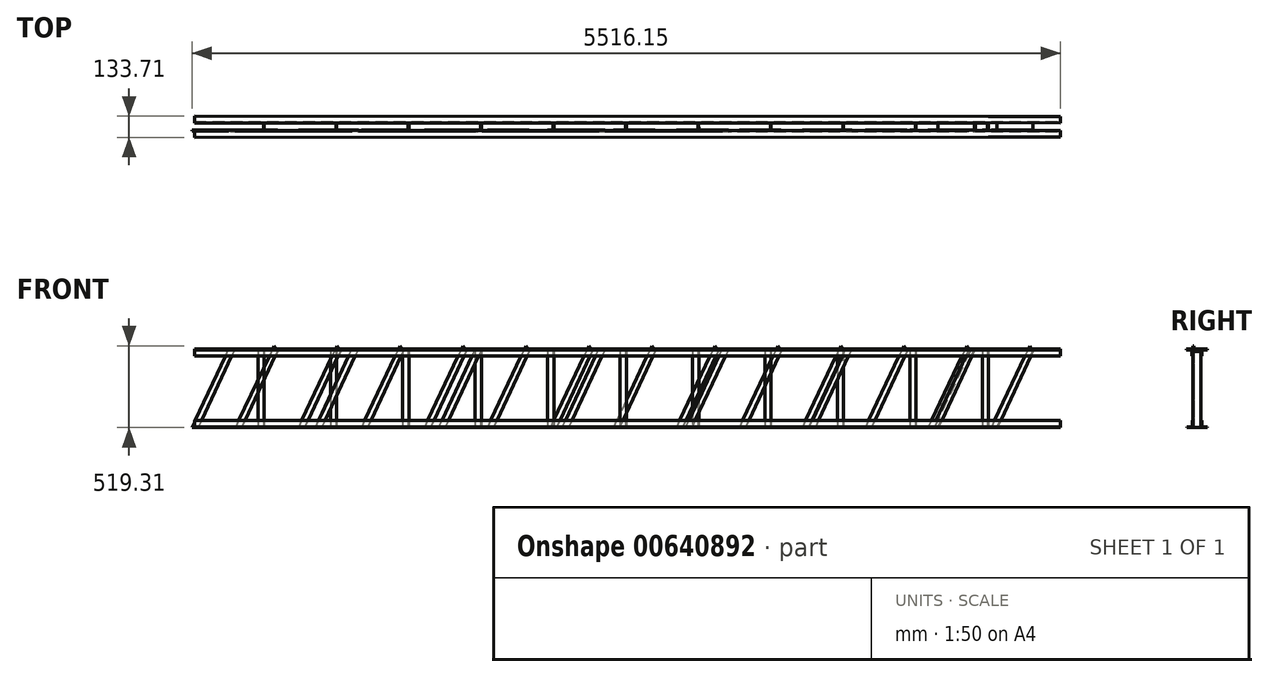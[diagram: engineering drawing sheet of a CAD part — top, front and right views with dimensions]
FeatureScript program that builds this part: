
annotation { "Feature Type Name" : "Feature", "Feature Type Description" : "" }
export const myFeature = defineFeature(function(context is Context, id is Id, definition is map)
    precondition{}
    {
        {
            var Q0;
            Q0=qCreatedBy(makeId("Top.planeOp"),FACE);
            var sketch = newSketch(context, id + "F0", { "sketchPlane" : qUnion([Q0])});
            skLineSegment(sketch, "E0.bottom", {"start": v(-72.3, 14.48) * mm, "end": v(5427.7, 14.48) * mm});
            skLineSegment(sketch, "E0.top", {"start": v(-72.3, -25.52) * mm, "end": v(5427.7, -25.52) * mm});
            skLineSegment(sketch, "E0.left", {"start": v(-72.3, 14.48) * mm, "end": v(-72.3, -25.52) * mm});
            skLineSegment(sketch, "E0.right", {"start": v(5427.7, 14.48) * mm, "end": v(5427.7, -25.52) * mm});
            skSolve(sketch);
        }
        {
            var Q0;
            Q0 = qSketchRegion(id + "F0", true);
            extrude(context, id + "F1", {"entities" : qUnion([Q0]), "depth" : 5 * mm, "offsetDistance" : 25.4 * mm});
        }
        {
            var Q0;
            Q0=makeQuery(id+"F1.opExtrude","CAP_FACE",FACE,{"disambiguationData":[OSD([sQuery(id+"F0.wireOp",EDGE,"E0.bottom"),sQuery(id+"F0.wireOp",EDGE,"E0.top"),sQuery(id+"F0.wireOp",EDGE,"E0.left"),sQuery(id+"F0.wireOp",EDGE,"E0.right")])],"isStart":false});
            var sketch = newSketch(context, id + "F2", { "sketchPlane" : qUnion([Q0])});
            skLineSegment(sketch, "E1.bottom", {"start": v(-72.3, -25.52) * mm, "end": v(5427.7, -25.52) * mm});
            skLineSegment(sketch, "E1.top", {"start": v(-72.3, -20.52) * mm, "end": v(5427.7, -20.52) * mm});
            skLineSegment(sketch, "E1.left", {"start": v(-72.3, -25.52) * mm, "end": v(-72.3, -20.52) * mm});
            skLineSegment(sketch, "E1.right", {"start": v(5427.7, -25.52) * mm, "end": v(5427.7, -20.52) * mm});
            skSolve(sketch);
        }
        {
            var Q0;
            Q0 = qSketchRegion(id + "F2", true);
            extrude(context, id + "F3", {"entities" : qUnion([Q0]), "operationType" : NewBodyOperationType.ADD, "depth" : 40 * mm, "offsetDistance" : 25.4 * mm});
        }
        {
            var Q0;
            Q0=makeQuery(id+"F3.boolean.opBoolean","MERGE",FACE,{"derivedFrom":[makeQuery(id+"F1.opExtrude","SWEPT_FACE",FACE,{"disambiguationData":[OSD([sQuery(id+"F0.wireOp",EDGE,"E0.top")])]}),makeQuery(id+"F3.opExtrude","SWEPT_FACE",FACE,{"disambiguationData":[OSD([sQuery(id+"F2.wireOp",EDGE,"E1.bottom")])]})]});
            cPlane(context, id + "F4", {"entities" : qUnion([Q0]), "cplaneType" : CPlaneType.OFFSET, "offset" : 25 * mm, "width" : 152.4 * mm, "height" : 152.4 * mm});
        }
        {
            var Q0;
            Q0=makeQuery(id+"F1.opExtrude","SWEPT_BODY",BODY,{"disambiguationData":[OSD([sQuery(id+"F0.wireOp",EDGE,"E0.bottom"),sQuery(id+"F0.wireOp",EDGE,"E0.top"),sQuery(id+"F0.wireOp",EDGE,"E0.left"),sQuery(id+"F0.wireOp",EDGE,"E0.right")])]});
            var Q1;
            Q1=qCreatedBy(id+"F4.planeOp",FACE);
            mirror(context, id + "F5", {"entities" : qUnion([Q0]), "mirrorPlane" : qUnion([Q1])});
        }
        {
            var Q0;
            Q0=makeQuery(id+"F5.opPattern","COPY",FACE,{"derivedFrom":makeQuery(id+"F3.boolean.opBoolean","MERGE",FACE,{"derivedFrom":[makeQuery(id+"F1.opExtrude","SWEPT_FACE",FACE,{"disambiguationData":[OSD([sQuery(id+"F0.wireOp",EDGE,"E0.top")])]}),makeQuery(id+"F3.opExtrude","SWEPT_FACE",FACE,{"disambiguationData":[OSD([sQuery(id+"F2.wireOp",EDGE,"E1.bottom")])]})]}),"instanceName":"1"});
            var sketch = newSketch(context, id + "F6", { "sketchPlane" : qUnion([Q0])});
            skLineSegment(sketch, "E2", {"start": v(-5233.44, 519.3) * mm, "end": v(-5253.8, 484.87) * mm});
            skLineSegment(sketch, "E3", {"start": v(-5253.8, 484.87) * mm, "end": v(-5027.7, 0) * mm});
            skLineSegment(sketch, "E4", {"start": v(-5027.7, 0) * mm, "end": v(-4987.7, 0) * mm});
            skLineSegment(sketch, "E5", {"start": v(-5233.44, 519.3) * mm, "end": v(-4987.7, 0) * mm});
            skLineSegment(sketch, "E6.1.0.0", {"start": v(-4853.8, 484.87) * mm, "end": v(-4627.7, 0) * mm});
            skLineSegment(sketch, "E6.1.0.1", {"start": v(-4833.44, 519.3) * mm, "end": v(-4587.7, 0) * mm});
            skLineSegment(sketch, "E6.1.0.2", {"start": v(-4833.44, 519.3) * mm, "end": v(-4853.8, 484.87) * mm});
            skLineSegment(sketch, "E6.1.0.3", {"start": v(-4627.7, 0) * mm, "end": v(-4587.7, 0) * mm});
            skLineSegment(sketch, "E6.2.0.0", {"start": v(-4453.8, 484.87) * mm, "end": v(-4227.7, 0) * mm});
            skLineSegment(sketch, "E6.2.0.1", {"start": v(-4433.44, 519.3) * mm, "end": v(-4187.7, 0) * mm});
            skLineSegment(sketch, "E6.2.0.2", {"start": v(-4433.44, 519.3) * mm, "end": v(-4453.8, 484.87) * mm});
            skLineSegment(sketch, "E6.2.0.3", {"start": v(-4227.7, 0) * mm, "end": v(-4187.7, 0) * mm});
            skLineSegment(sketch, "E6.3.0.0", {"start": v(-4053.8, 484.87) * mm, "end": v(-3827.7, 0) * mm});
            skLineSegment(sketch, "E6.3.0.1", {"start": v(-4033.44, 519.3) * mm, "end": v(-3787.7, 0) * mm});
            skLineSegment(sketch, "E6.3.0.2", {"start": v(-4033.44, 519.3) * mm, "end": v(-4053.8, 484.87) * mm});
            skLineSegment(sketch, "E6.3.0.3", {"start": v(-3827.7, 0) * mm, "end": v(-3787.7, 0) * mm});
            skLineSegment(sketch, "E6.4.0.0", {"start": v(-3653.8, 484.87) * mm, "end": v(-3427.7, 0) * mm});
            skLineSegment(sketch, "E6.4.0.1", {"start": v(-3633.44, 519.3) * mm, "end": v(-3387.7, 0) * mm});
            skLineSegment(sketch, "E6.4.0.2", {"start": v(-3633.44, 519.3) * mm, "end": v(-3653.8, 484.87) * mm});
            skLineSegment(sketch, "E6.4.0.3", {"start": v(-3427.7, 0) * mm, "end": v(-3387.7, 0) * mm});
            skLineSegment(sketch, "E6.5.0.0", {"start": v(-3253.8, 484.87) * mm, "end": v(-3027.7, 0) * mm});
            skLineSegment(sketch, "E6.5.0.1", {"start": v(-3233.44, 519.3) * mm, "end": v(-2987.7, 0) * mm});
            skLineSegment(sketch, "E6.5.0.2", {"start": v(-3233.44, 519.3) * mm, "end": v(-3253.8, 484.87) * mm});
            skLineSegment(sketch, "E6.5.0.3", {"start": v(-3027.7, 0) * mm, "end": v(-2987.7, 0) * mm});
            skLineSegment(sketch, "E6.6.0.0", {"start": v(-2853.8, 484.87) * mm, "end": v(-2627.7, 0) * mm});
            skLineSegment(sketch, "E6.6.0.1", {"start": v(-2833.44, 519.3) * mm, "end": v(-2587.7, 0) * mm});
            skLineSegment(sketch, "E6.6.0.2", {"start": v(-2833.44, 519.3) * mm, "end": v(-2853.8, 484.87) * mm});
            skLineSegment(sketch, "E6.6.0.3", {"start": v(-2627.7, 0) * mm, "end": v(-2587.7, 0) * mm});
            skLineSegment(sketch, "E6.7.0.0", {"start": v(-2453.8, 484.87) * mm, "end": v(-2227.7, 0) * mm});
            skLineSegment(sketch, "E6.7.0.1", {"start": v(-2433.44, 519.3) * mm, "end": v(-2187.7, 0) * mm});
            skLineSegment(sketch, "E6.7.0.2", {"start": v(-2433.44, 519.3) * mm, "end": v(-2453.8, 484.87) * mm});
            skLineSegment(sketch, "E6.7.0.3", {"start": v(-2227.7, 0) * mm, "end": v(-2187.7, 0) * mm});
            skLineSegment(sketch, "E6.8.0.0", {"start": v(-2053.8, 484.87) * mm, "end": v(-1827.7, 0) * mm});
            skLineSegment(sketch, "E6.8.0.1", {"start": v(-2033.44, 519.3) * mm, "end": v(-1787.7, 0) * mm});
            skLineSegment(sketch, "E6.8.0.2", {"start": v(-2033.44, 519.3) * mm, "end": v(-2053.8, 484.87) * mm});
            skLineSegment(sketch, "E6.8.0.3", {"start": v(-1827.7, 0) * mm, "end": v(-1787.7, 0) * mm});
            skLineSegment(sketch, "E6.9.0.0", {"start": v(-1653.8, 484.87) * mm, "end": v(-1427.7, 0) * mm});
            skLineSegment(sketch, "E6.9.0.1", {"start": v(-1633.44, 519.3) * mm, "end": v(-1387.7, 0) * mm});
            skLineSegment(sketch, "E6.9.0.2", {"start": v(-1633.44, 519.3) * mm, "end": v(-1653.8, 484.87) * mm});
            skLineSegment(sketch, "E6.9.0.3", {"start": v(-1427.7, 0) * mm, "end": v(-1387.7, 0) * mm});
            skLineSegment(sketch, "E6.10.0.0", {"start": v(-1253.8, 484.87) * mm, "end": v(-1027.7, 0) * mm});
            skLineSegment(sketch, "E6.10.0.1", {"start": v(-1233.44, 519.3) * mm, "end": v(-987.7, 0) * mm});
            skLineSegment(sketch, "E6.10.0.2", {"start": v(-1233.44, 519.3) * mm, "end": v(-1253.8, 484.87) * mm});
            skLineSegment(sketch, "E6.10.0.3", {"start": v(-1027.7, 0) * mm, "end": v(-987.7, 0) * mm});
            skLineSegment(sketch, "E6.11.0.0", {"start": v(-853.8, 484.87) * mm, "end": v(-627.7, 0) * mm});
            skLineSegment(sketch, "E6.11.0.1", {"start": v(-833.44, 519.3) * mm, "end": v(-587.7, 0) * mm});
            skLineSegment(sketch, "E6.11.0.2", {"start": v(-833.44, 519.3) * mm, "end": v(-853.8, 484.87) * mm});
            skLineSegment(sketch, "E6.11.0.3", {"start": v(-627.7, 0) * mm, "end": v(-587.7, 0) * mm});
            skLineSegment(sketch, "E6.12.0.0", {"start": v(-453.8, 484.87) * mm, "end": v(-227.7, 0) * mm});
            skLineSegment(sketch, "E6.12.0.1", {"start": v(-433.44, 519.3) * mm, "end": v(-187.7, 0) * mm});
            skLineSegment(sketch, "E6.12.0.2", {"start": v(-433.44, 519.3) * mm, "end": v(-453.8, 484.87) * mm});
            skLineSegment(sketch, "E6.12.0.3", {"start": v(-227.7, 0) * mm, "end": v(-187.7, 0) * mm});
            skLineSegment(sketch, "E6.direction1", {"start": v(-5027.7, 0) * mm, "end": v(-4627.7, 0) * mm, "construction": true});
            skSolve(sketch);
        }
        {
            var Q0;
            Q0 = qSketchRegion(id + "F6", true);
            extrude(context, id + "F7", {"entities" : qUnion([Q0]), "operationType" : NewBodyOperationType.ADD, "depth" : 5 * mm, "offsetDistance" : 25.4 * mm});
        }
        {
            var Q0;
            Q0=makeQuery(id+"F7.opExtrude","CAP_FACE",FACE,{"disambiguationData":[OSD([sQuery(id+"F6.wireOp",EDGE,"E2"),sQuery(id+"F6.wireOp",EDGE,"E3"),sQuery(id+"F6.wireOp",EDGE,"E4"),sQuery(id+"F6.wireOp",EDGE,"E5")])],"isStart":false});
            var sketch = newSketch(context, id + "F8", { "sketchPlane" : qUnion([Q0])});
            skLineSegment(sketch, "E7", {"start": v(-5253.8, 484.87) * mm, "end": v(-5251.25, 489.18) * mm});
            skLineSegment(sketch, "E8", {"start": v(-5251.25, 489.18) * mm, "end": v(-5022.7, 0) * mm});
            skLineSegment(sketch, "E9", {"start": v(-5022.7, 0) * mm, "end": v(-5027.7, 0) * mm});
            skLineSegment(sketch, "E10", {"start": v(-5027.7, 0) * mm, "end": v(-5253.8, 484.87) * mm});
            skSolve(sketch);
        }
        {
            var Q0;
            Q0 = qSketchRegion(id + "F8", true);
            var Q1;
            Q1=makeQuery(id+"F3.boolean.opBoolean","MERGE",FACE,{"derivedFrom":[makeQuery(id+"F1.opExtrude","SWEPT_FACE",FACE,{"disambiguationData":[OSD([sQuery(id+"F0.wireOp",EDGE,"E0.top")])]}),makeQuery(id+"F3.opExtrude","SWEPT_FACE",FACE,{"disambiguationData":[OSD([sQuery(id+"F2.wireOp",EDGE,"E1.bottom")])]})]});
            extrude(context, id + "F9", {"entities" : qUnion([Q0]), "operationType" : NewBodyOperationType.ADD, "endBound" : BoundingType.UP_TO_SURFACE, "depth" : 25 * mm, "endBoundEntityFace" : qUnion([Q1]), "offsetDistance" : 25.4 * mm});
        }
        {
            var Q0;
            Q0=makeQuery(id+"F1.opExtrude","CAP_FACE",FACE,{"disambiguationData":[OSD([sQuery(id+"F0.wireOp",EDGE,"E0.bottom"),sQuery(id+"F0.wireOp",EDGE,"E0.top"),sQuery(id+"F0.wireOp",EDGE,"E0.left"),sQuery(id+"F0.wireOp",EDGE,"E0.right")])],"isStart":true});
            var sketch = newSketch(context, id + "F10", { "sketchPlane" : qUnion([Q0])});
            skLineSegment(sketch, "E11.bottom", {"start": v(4970.5, 75.52) * mm, "end": v(4930.5, 75.54) * mm});
            skLineSegment(sketch, "E11.left", {"start": v(4970.5, 75.52) * mm, "end": v(4970.22, 25.52) * mm});
            skLineSegment(sketch, "E11.right", {"start": v(4930.5, 75.54) * mm, "end": v(4930.47, 70.54) * mm});
            skLineSegment(sketch, "E12", {"start": v(4930.47, 70.54) * mm, "end": v(4965.22, 70.35) * mm});
            skLineSegment(sketch, "E13", {"start": v(4965.22, 70.35) * mm, "end": v(4965.22, 25.52) * mm});
            skLineSegment(sketch, "E14", {"start": v(4965.22, 25.52) * mm, "end": v(4970.22, 25.52) * mm});
            skLineSegment(sketch, "E15.1.0.0", {"start": v(4470.5, 75.54) * mm, "end": v(4470.47, 70.54) * mm});
            skLineSegment(sketch, "E15.1.0.1", {"start": v(4510.5, 75.52) * mm, "end": v(4470.5, 75.54) * mm});
            skLineSegment(sketch, "E15.1.0.2", {"start": v(4470.47, 70.54) * mm, "end": v(4505.22, 70.35) * mm});
            skLineSegment(sketch, "E15.1.0.3", {"start": v(4505.22, 70.35) * mm, "end": v(4505.22, 25.52) * mm});
            skLineSegment(sketch, "E15.1.0.4", {"start": v(4510.5, 75.52) * mm, "end": v(4510.22, 25.52) * mm});
            skLineSegment(sketch, "E15.1.0.5", {"start": v(4505.22, 25.52) * mm, "end": v(4510.22, 25.52) * mm});
            skLineSegment(sketch, "E15.2.0.0", {"start": v(4010.5, 75.54) * mm, "end": v(4010.47, 70.54) * mm});
            skLineSegment(sketch, "E15.2.0.1", {"start": v(4050.5, 75.52) * mm, "end": v(4010.5, 75.54) * mm});
            skLineSegment(sketch, "E15.2.0.2", {"start": v(4010.47, 70.54) * mm, "end": v(4045.22, 70.35) * mm});
            skLineSegment(sketch, "E15.2.0.3", {"start": v(4045.22, 70.35) * mm, "end": v(4045.22, 25.52) * mm});
            skLineSegment(sketch, "E15.2.0.4", {"start": v(4050.5, 75.52) * mm, "end": v(4050.22, 25.52) * mm});
            skLineSegment(sketch, "E15.2.0.5", {"start": v(4045.22, 25.52) * mm, "end": v(4050.22, 25.52) * mm});
            skLineSegment(sketch, "E15.3.0.0", {"start": v(3550.5, 75.54) * mm, "end": v(3550.47, 70.54) * mm});
            skLineSegment(sketch, "E15.3.0.1", {"start": v(3590.5, 75.52) * mm, "end": v(3550.5, 75.54) * mm});
            skLineSegment(sketch, "E15.3.0.2", {"start": v(3550.47, 70.54) * mm, "end": v(3585.22, 70.35) * mm});
            skLineSegment(sketch, "E15.3.0.3", {"start": v(3585.22, 70.35) * mm, "end": v(3585.22, 25.52) * mm});
            skLineSegment(sketch, "E15.3.0.4", {"start": v(3590.5, 75.52) * mm, "end": v(3590.22, 25.52) * mm});
            skLineSegment(sketch, "E15.3.0.5", {"start": v(3585.22, 25.52) * mm, "end": v(3590.22, 25.52) * mm});
            skLineSegment(sketch, "E15.4.0.0", {"start": v(3090.5, 75.54) * mm, "end": v(3090.47, 70.54) * mm});
            skLineSegment(sketch, "E15.4.0.1", {"start": v(3130.5, 75.52) * mm, "end": v(3090.5, 75.54) * mm});
            skLineSegment(sketch, "E15.4.0.2", {"start": v(3090.47, 70.54) * mm, "end": v(3125.22, 70.35) * mm});
            skLineSegment(sketch, "E15.4.0.3", {"start": v(3125.22, 70.35) * mm, "end": v(3125.22, 25.52) * mm});
            skLineSegment(sketch, "E15.4.0.4", {"start": v(3130.5, 75.52) * mm, "end": v(3130.22, 25.52) * mm});
            skLineSegment(sketch, "E15.4.0.5", {"start": v(3125.22, 25.52) * mm, "end": v(3130.22, 25.52) * mm});
            skLineSegment(sketch, "E15.5.0.0", {"start": v(2630.5, 75.54) * mm, "end": v(2630.47, 70.54) * mm});
            skLineSegment(sketch, "E15.5.0.1", {"start": v(2670.5, 75.52) * mm, "end": v(2630.5, 75.54) * mm});
            skLineSegment(sketch, "E15.5.0.2", {"start": v(2630.47, 70.54) * mm, "end": v(2665.22, 70.35) * mm});
            skLineSegment(sketch, "E15.5.0.3", {"start": v(2665.22, 70.35) * mm, "end": v(2665.22, 25.52) * mm});
            skLineSegment(sketch, "E15.5.0.4", {"start": v(2670.5, 75.52) * mm, "end": v(2670.22, 25.52) * mm});
            skLineSegment(sketch, "E15.5.0.5", {"start": v(2665.22, 25.52) * mm, "end": v(2670.22, 25.52) * mm});
            skLineSegment(sketch, "E15.6.0.0", {"start": v(2170.5, 75.54) * mm, "end": v(2170.47, 70.54) * mm});
            skLineSegment(sketch, "E15.6.0.1", {"start": v(2210.5, 75.52) * mm, "end": v(2170.5, 75.54) * mm});
            skLineSegment(sketch, "E15.6.0.2", {"start": v(2170.47, 70.54) * mm, "end": v(2205.22, 70.35) * mm});
            skLineSegment(sketch, "E15.6.0.3", {"start": v(2205.22, 70.35) * mm, "end": v(2205.22, 25.52) * mm});
            skLineSegment(sketch, "E15.6.0.4", {"start": v(2210.5, 75.52) * mm, "end": v(2210.22, 25.52) * mm});
            skLineSegment(sketch, "E15.6.0.5", {"start": v(2205.22, 25.52) * mm, "end": v(2210.22, 25.52) * mm});
            skLineSegment(sketch, "E15.7.0.0", {"start": v(1710.5, 75.54) * mm, "end": v(1710.47, 70.54) * mm});
            skLineSegment(sketch, "E15.7.0.1", {"start": v(1750.5, 75.52) * mm, "end": v(1710.5, 75.54) * mm});
            skLineSegment(sketch, "E15.7.0.2", {"start": v(1710.47, 70.54) * mm, "end": v(1745.22, 70.35) * mm});
            skLineSegment(sketch, "E15.7.0.3", {"start": v(1745.22, 70.35) * mm, "end": v(1745.22, 25.52) * mm});
            skLineSegment(sketch, "E15.7.0.4", {"start": v(1750.5, 75.52) * mm, "end": v(1750.22, 25.52) * mm});
            skLineSegment(sketch, "E15.7.0.5", {"start": v(1745.22, 25.52) * mm, "end": v(1750.22, 25.52) * mm});
            skLineSegment(sketch, "E15.8.0.0", {"start": v(1250.5, 75.54) * mm, "end": v(1250.47, 70.54) * mm});
            skLineSegment(sketch, "E15.8.0.1", {"start": v(1290.5, 75.52) * mm, "end": v(1250.5, 75.54) * mm});
            skLineSegment(sketch, "E15.8.0.2", {"start": v(1250.47, 70.54) * mm, "end": v(1285.22, 70.35) * mm});
            skLineSegment(sketch, "E15.8.0.3", {"start": v(1285.22, 70.35) * mm, "end": v(1285.22, 25.52) * mm});
            skLineSegment(sketch, "E15.8.0.4", {"start": v(1290.5, 75.52) * mm, "end": v(1290.22, 25.52) * mm});
            skLineSegment(sketch, "E15.8.0.5", {"start": v(1285.22, 25.52) * mm, "end": v(1290.22, 25.52) * mm});
            skLineSegment(sketch, "E15.9.0.0", {"start": v(790.5, 75.54) * mm, "end": v(790.47, 70.54) * mm});
            skLineSegment(sketch, "E15.9.0.1", {"start": v(830.5, 75.52) * mm, "end": v(790.5, 75.54) * mm});
            skLineSegment(sketch, "E15.9.0.2", {"start": v(790.47, 70.54) * mm, "end": v(825.22, 70.35) * mm});
            skLineSegment(sketch, "E15.9.0.3", {"start": v(825.22, 70.35) * mm, "end": v(825.22, 25.52) * mm});
            skLineSegment(sketch, "E15.9.0.4", {"start": v(830.5, 75.52) * mm, "end": v(830.22, 25.52) * mm});
            skLineSegment(sketch, "E15.9.0.5", {"start": v(825.22, 25.52) * mm, "end": v(830.22, 25.52) * mm});
            skLineSegment(sketch, "E15.10.0.0", {"start": v(330.5, 75.54) * mm, "end": v(330.47, 70.54) * mm});
            skLineSegment(sketch, "E15.10.0.1", {"start": v(370.5, 75.52) * mm, "end": v(330.5, 75.54) * mm});
            skLineSegment(sketch, "E15.10.0.2", {"start": v(330.47, 70.54) * mm, "end": v(365.22, 70.35) * mm});
            skLineSegment(sketch, "E15.10.0.3", {"start": v(365.22, 70.35) * mm, "end": v(365.22, 25.52) * mm});
            skLineSegment(sketch, "E15.10.0.4", {"start": v(370.5, 75.52) * mm, "end": v(370.22, 25.52) * mm});
            skLineSegment(sketch, "E15.10.0.5", {"start": v(365.22, 25.52) * mm, "end": v(370.22, 25.52) * mm});
            skLineSegment(sketch, "E15.direction1", {"start": v(4930.47, 70.54) * mm, "end": v(4470.47, 70.54) * mm, "construction": true});
            skSolve(sketch);
        }
        {
            var Q0;
            Q0=makeQuery(id+"F10.imprint","IMPRINT",FACE,{"disambiguationData":[TD([[makeQuery(id+"F10.imprint","IMPRINT",EDGE,{"derivedFrom":sQuery(id+"F10.wireOp",EDGE,"E11.bottom")}),1.0]])]});
            extrude(context, id + "F11", {"entities" : qUnion([Q0]), "oppositeDirection" : true, "depth" : 500 * mm, "offsetDistance" : 25.4 * mm});
        }
        {
            var Q0;
            Q0=makeQuery(id+"F11.opExtrude","SWEPT_FACE",FACE,{"disambiguationData":[OSD([sQuery(id+"F10.wireOp",EDGE,"E11.bottom")])]});
            var sketch = newSketch(context, id + "F12", { "sketchPlane" : qUnion([Q0])});
            skLineSegment(sketch, "E16.bottom", {"start": v(-72.33, 500) * mm, "end": v(5427.67, 500) * mm});
            skLineSegment(sketch, "E16.top", {"start": v(-72.33, 495) * mm, "end": v(5427.67, 495) * mm});
            skLineSegment(sketch, "E16.left", {"start": v(-72.33, 500) * mm, "end": v(-72.33, 495) * mm});
            skLineSegment(sketch, "E16.right", {"start": v(5427.67, 500) * mm, "end": v(5427.67, 495) * mm});
            skSolve(sketch);
        }
        {
            var Q0;
            Q0 = qSketchRegion(id + "F12", true);
            extrude(context, id + "F13", {"entities" : qUnion([Q0]), "depth" : 40 * mm, "offsetDistance" : 25.4 * mm});
        }
        {
            var Q0;
            Q0=makeQuery(id+"F13.opExtrude","SWEPT_FACE",FACE,{"disambiguationData":[OSD([sQuery(id+"F12.wireOp",EDGE,"E16.top")])]});
            var sketch = newSketch(context, id + "F14", { "sketchPlane" : qUnion([Q0])});
            skLineSegment(sketch, "E17.bottom", {"start": v(-72.3, 77.38) * mm, "end": v(5427.7, 77.38) * mm});
            skLineSegment(sketch, "E17.top", {"start": v(-72.3, 82.38) * mm, "end": v(5427.7, 82.38) * mm});
            skLineSegment(sketch, "E17.left", {"start": v(-72.3, 77.38) * mm, "end": v(-72.3, 82.38) * mm});
            skLineSegment(sketch, "E17.right", {"start": v(5427.7, 77.38) * mm, "end": v(5427.7, 82.38) * mm});
            skSolve(sketch);
        }
        {
            var Q0;
            Q0 = qSketchRegion(id + "F14", true);
            extrude(context, id + "F15", {"entities" : qUnion([Q0]), "operationType" : NewBodyOperationType.ADD, "depth" : 40 * mm, "offsetDistance" : 25.4 * mm});
        }
        {
            var Q0;
            Q0=makeQuery(id+"F13.opExtrude","SWEPT_BODY",BODY,{"disambiguationData":[OSD([sQuery(id+"F12.wireOp",EDGE,"E16.bottom"),sQuery(id+"F12.wireOp",EDGE,"E16.top"),sQuery(id+"F12.wireOp",EDGE,"E16.left"),sQuery(id+"F12.wireOp",EDGE,"E16.right")])]});
            var Q1;
            Q1=qCreatedBy(id+"F4.planeOp",FACE);
            mirror(context, id + "F16", {"operationType" : NewBodyOperationType.ADD, "entities" : qUnion([Q0]), "mirrorPlane" : qUnion([Q1])});
        }
        {
            var Q0;
            {var subQ0=sQuery(id+"F12.wireOp",EDGE,"E16.top");var subQ1=sQuery(id+"F12.wireOp",EDGE,"E16.bottom");var subQ2=sQuery(id+"F12.wireOp",EDGE,"E16.left");Q0=makeQuery(id+"F16.boolean.opBoolean","SPLIT",FACE,{"disambiguationData":[TD([makeQuery(id+"F7.opExtrude","SWEPT_FACE",FACE,{"disambiguationData":[OSD([sQuery(id+"F6.wireOp",EDGE,"E5")])]})])],"derivedFrom":makeQuery(id+"F13.opExtrude","CAP_FACE",FACE,{"disambiguationData":[OSD([subQ1,subQ0,subQ2,sQuery(id+"F12.wireOp",EDGE,"E16.right")])],"isStart":true})});}
            var sketch = newSketch(context, id + "F17", { "sketchPlane" : qUnion([Q0])});
            skLineSegment(sketch, "E18", {"start": v(-4887.48, 500) * mm, "end": v(-4654.33, 0) * mm});
            skLineSegment(sketch, "E19", {"start": v(-4654.33, 0) * mm, "end": v(-4614.33, 0) * mm});
            skLineSegment(sketch, "E20", {"start": v(-4614.33, 0) * mm, "end": v(-4847.48, 500) * mm});
            skLineSegment(sketch, "E21", {"start": v(-4847.48, 500) * mm, "end": v(-4887.48, 500) * mm});
            skLineSegment(sketch, "E22.1.0.0", {"start": v(-3830.53, 0) * mm, "end": v(-4063.68, 500) * mm});
            skLineSegment(sketch, "E22.1.0.1", {"start": v(-3870.53, 0) * mm, "end": v(-3830.53, 0) * mm});
            skLineSegment(sketch, "E22.1.0.2", {"start": v(-4103.68, 500) * mm, "end": v(-3870.53, 0) * mm});
            skLineSegment(sketch, "E22.1.0.3", {"start": v(-4063.68, 500) * mm, "end": v(-4103.68, 500) * mm});
            skLineSegment(sketch, "E22.2.0.0", {"start": v(-3046.73, 0) * mm, "end": v(-3279.88, 500) * mm});
            skLineSegment(sketch, "E22.2.0.1", {"start": v(-3086.73, 0) * mm, "end": v(-3046.73, 0) * mm});
            skLineSegment(sketch, "E22.2.0.2", {"start": v(-3319.88, 500) * mm, "end": v(-3086.73, 0) * mm});
            skLineSegment(sketch, "E22.2.0.3", {"start": v(-3279.88, 500) * mm, "end": v(-3319.88, 500) * mm});
            skLineSegment(sketch, "E22.3.0.0", {"start": v(-2262.93, 0) * mm, "end": v(-2496.08, 500) * mm});
            skLineSegment(sketch, "E22.3.0.1", {"start": v(-2302.93, 0) * mm, "end": v(-2262.93, 0) * mm});
            skLineSegment(sketch, "E22.3.0.2", {"start": v(-2536.08, 500) * mm, "end": v(-2302.93, 0) * mm});
            skLineSegment(sketch, "E22.3.0.3", {"start": v(-2496.08, 500) * mm, "end": v(-2536.08, 500) * mm});
            skLineSegment(sketch, "E22.4.0.0", {"start": v(-1479.13, 0) * mm, "end": v(-1712.28, 500) * mm});
            skLineSegment(sketch, "E22.4.0.1", {"start": v(-1519.13, 0) * mm, "end": v(-1479.13, 0) * mm});
            skLineSegment(sketch, "E22.4.0.2", {"start": v(-1752.28, 500) * mm, "end": v(-1519.13, 0) * mm});
            skLineSegment(sketch, "E22.4.0.3", {"start": v(-1712.28, 500) * mm, "end": v(-1752.28, 500) * mm});
            skLineSegment(sketch, "E22.5.0.0", {"start": v(-695.33, 0) * mm, "end": v(-928.48, 500) * mm});
            skLineSegment(sketch, "E22.5.0.1", {"start": v(-735.33, 0) * mm, "end": v(-695.33, 0) * mm});
            skLineSegment(sketch, "E22.5.0.2", {"start": v(-968.48, 500) * mm, "end": v(-735.33, 0) * mm});
            skLineSegment(sketch, "E22.5.0.3", {"start": v(-928.48, 500) * mm, "end": v(-968.48, 500) * mm});
            skLineSegment(sketch, "E22.6.0.0", {"start": v(88.47, 0) * mm, "end": v(-144.68, 500) * mm});
            skLineSegment(sketch, "E22.6.0.1", {"start": v(48.47, 0) * mm, "end": v(88.47, 0) * mm});
            skLineSegment(sketch, "E22.6.0.2", {"start": v(-184.68, 500) * mm, "end": v(48.47, 0) * mm});
            skLineSegment(sketch, "E22.6.0.3", {"start": v(-144.68, 500) * mm, "end": v(-184.68, 500) * mm});
            skLineSegment(sketch, "E22.direction1", {"start": v(-4614.33, 0) * mm, "end": v(-3830.53, 0) * mm, "construction": true});
            skSolve(sketch);
        }
        {
            var Q0;
            Q0 = qSketchRegion(id + "F17", true);
            extrude(context, id + "F18", {"entities" : qUnion([Q0]), "operationType" : NewBodyOperationType.ADD, "depth" : 5 * mm, "offsetDistance" : 25.4 * mm});
        }
        {
            var Q0;
            Q0=makeQuery(id+"F18.opExtrude","CAP_FACE",FACE,{"disambiguationData":[OSD([sQuery(id+"F17.wireOp",EDGE,"E18"),sQuery(id+"F17.wireOp",EDGE,"E19"),sQuery(id+"F17.wireOp",EDGE,"E20"),sQuery(id+"F17.wireOp",EDGE,"E21")])],"isStart":false});
            var sketch = newSketch(context, id + "F19", { "sketchPlane" : qUnion([Q0])});
            skLineSegment(sketch, "E23", {"start": v(-4882.48, 500) * mm, "end": v(-4887.48, 500) * mm});
            skLineSegment(sketch, "E24", {"start": v(-4887.48, 500) * mm, "end": v(-4654.33, 0) * mm});
            skLineSegment(sketch, "E25", {"start": v(-4654.33, 0) * mm, "end": v(-4649.33, 0) * mm});
            skLineSegment(sketch, "E26", {"start": v(-4649.33, 0) * mm, "end": v(-4882.48, 500) * mm});
            skSolve(sketch);
        }
        {
            var Q0;
            Q0 = qSketchRegion(id + "F19", true);
            var Q1;
            Q1=makeQuery(id+"F3.boolean.opBoolean","MERGE",FACE,{"derivedFrom":[makeQuery(id+"F1.opExtrude","SWEPT_FACE",FACE,{"disambiguationData":[OSD([sQuery(id+"F0.wireOp",EDGE,"E0.top")])]}),makeQuery(id+"F3.opExtrude","SWEPT_FACE",FACE,{"disambiguationData":[OSD([sQuery(id+"F2.wireOp",EDGE,"E1.bottom")])]})]});
            extrude(context, id + "F20", {"entities" : qUnion([Q0]), "endBound" : BoundingType.UP_TO_SURFACE, "depth" : 25.4 * mm, "endBoundEntityFace" : qUnion([Q1]), "offsetDistance" : 25.4 * mm});
        }
        {
            var Q0;
            Q0 = qSketchRegion(id + "F10", true);
            extrude(context, id + "F21", {"entities" : qUnion([Q0]), "oppositeDirection" : true, "depth" : 500 * mm, "offsetDistance" : 25.4 * mm});
        }
    });
